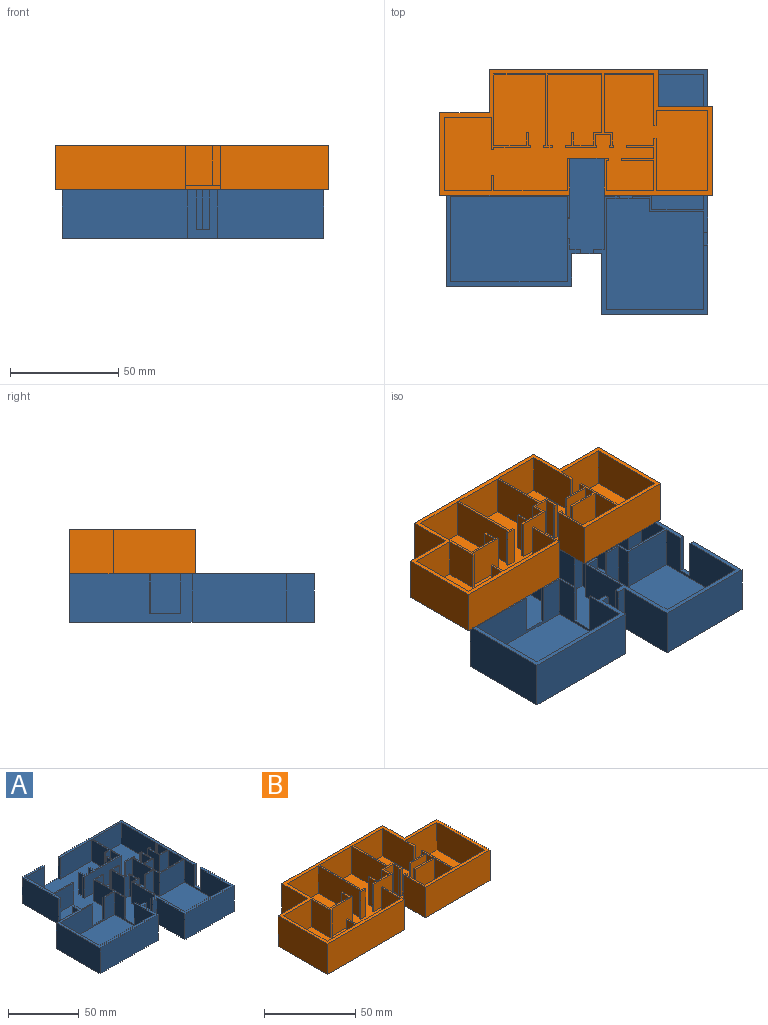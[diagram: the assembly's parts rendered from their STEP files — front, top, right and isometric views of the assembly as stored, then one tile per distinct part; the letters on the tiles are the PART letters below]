
ASSEMBLY  parts=2 mates=1
PART A: 128 faces, bbox 121x113x22.4 mm
  f0: plane 97x85mm, normal (0,0,1), area 5730mm2, adj f5,f6,f11,f17,f18,f19,f20,f21
  f1: plane 6x2mm, normal (0,0,1), area 12mm2, adj f4,f13,f14,f49
  f2: plane 28x22.4mm, normal (-1,0,0), area 627.2mm2, adj f3,f11,f12,f35
  f3: plane 49x22.4mm, normal (0,-1,0), area 1097.6mm2, adj f2,f4,f12,f35
  f4: plane 113x22.4mm, normal (1,0,0), area 2420.8mm2, adj f1,f3,f5,f12,f13,f35,f49,f107
  f5: plane 99x22.4mm, normal (0,1,0), area 1941.6mm2, adj f0,f4,f6,f12,f50,f107,f109,f116
  f6: plane 56.5x22.4mm, normal (-1,0,0), area 1008mm2, adj f0,f5,f7,f12,f37,f48,f110,f116
  f7: plane 22.4x22mm, normal (0,1,0), area 492.8mm2, adj f6,f8,f12,f48
  f8: plane 43.5x22.4mm, normal (-1,0,0), area 974.4mm2, adj f7,f9,f12,f48
  f9: plane 58x22.4mm, normal (0,-1,0), area 1299.2mm2, adj f8,f10,f12,f48
  f10: plane 22.4x15mm, normal (1,0,0), area 336mm2, adj f9,f11,f12,f48
  f11: plane 22.4x14mm, normal (0,-1,0), area 203.2mm2, adj f0,f2,f10,f12,f34,f35,f38,f48
  f12: plane 121x113mm, normal (0,0,-1), area 11284mm2, adj f2,f3,f4,f5,f6,f7,f8,f9
  f13: plane 18.4x2mm, normal (0,1,0), area 36.8mm2, adj f1,f4,f14,f35
  f14: plane 45.5x19.8mm, normal (-1,0,0), area 790.5mm2, adj f1,f13,f15,f35,f49,f106,f107,f126
  f15: plane 45x19.8mm, normal (0,1,0), area 891mm2, adj f14,f16,f35,f126
  f16: plane 51.5x19.8mm, normal (1,0,0), area 1019.7mm2, adj f15,f17,f35,f126
  f17: plane 20x19.8mm, normal (0,-1,0), area 285.6mm2, adj f0,f16,f18,f35,f104,f105,f107,f126
  f18: plane 18.4x1mm, normal (1,0,0), area 18.4mm2, adj f0,f17,f19,f35
  f19: plane 18.4x1mm, normal (0,1,0), area 18.4mm2, adj f0,f18,f20,f35
  f20: plane 18.4x8mm, normal (1,0,0), area 147.2mm2, adj f0,f19,f21,f35
  f21: plane 18.4x5mm, normal (0,1,0), area 92mm2, adj f0,f20,f22,f35
  f22: plane 18.4x12mm, normal (1,0,0), area 220.8mm2, adj f0,f21,f23,f35
  f23: plane 18.4x7mm, normal (0,-1,0), area 128.8mm2, adj f0,f22,f24,f35
  f24: plane 18.4x1mm, normal (1,0,0), area 18.4mm2, adj f0,f23,f25,f35
  f25: plane 18.4x9mm, normal (0,1,0), area 165.6mm2, adj f0,f24,f26,f35
  f26: plane 18.4x1mm, normal (-1,0,0), area 18.4mm2, adj f0,f25,f27,f35
  f27: plane 18.4x1mm, normal (0,-1,0), area 18.4mm2, adj f0,f26,f28,f35
  f28: plane 18.4x13mm, normal (-1,0,0), area 239.2mm2, adj f0,f27,f29,f35
  f29: plane 18.4x5mm, normal (0,-1,0), area 92mm2, adj f0,f28,f30,f35
  f30: plane 18.4x7mm, normal (-1,0,0), area 128.8mm2, adj f0,f29,f31,f35
  f31: plane 18.4x5mm, normal (0,1,0), area 92mm2, adj f0,f30,f32,f35
  f32: plane 24.5x18.4mm, normal (-1,0,0), area 450.8mm2, adj f0,f31,f33,f35
  f33: plane 18.4x5mm, normal (0,1,0), area 92mm2, adj f0,f32,f34,f35
  f34: plane 18.4x2mm, normal (-1,0,0), area 36.8mm2, adj f0,f11,f33,f35
  f35: plane 75.5x53mm, normal (0,0,1), area 286.5mm2, adj f2,f3,f4,f11,f13,f14,f15,f16
  f36: plane 18.4x6.5mm, normal (1,0,0), area 119.6mm2, adj f0,f37,f47,f48
  f37: plane 18.4x2mm, normal (0,1,0), area 36.8mm2, adj f0,f6,f36,f48
  f38: plane 18.4x2mm, normal (1,0,0), area 36.8mm2, adj f0,f11,f39,f48
  f39: plane 18.4x5mm, normal (0,1,0), area 92mm2, adj f0,f38,f40,f48
  f40: plane 18.4x5mm, normal (1,0,0), area 92mm2, adj f0,f39,f41,f48
  f41: plane 18.4x1mm, normal (0,1,0), area 18.4mm2, adj f0,f40,f42,f48
  f42: plane 39.5x19.8mm, normal (-1,0,0), area 607.3mm2, adj f0,f41,f43,f45,f48,f117,f125,f127
  f43: plane 54x19.8mm, normal (0,1,0), area 1069.2mm2, adj f42,f44,f48,f127
  f44: plane 39.5x19.8mm, normal (1,0,0), area 782.1mm2, adj f43,f45,f48,f127
  f45: plane 54x19.8mm, normal (0,-1,0), area 866.8mm2, adj f0,f42,f44,f46,f48,f124,f125,f127
  f46: plane 18.4x1mm, normal (1,0,0), area 18.4mm2, adj f0,f45,f47,f48
  f47: plane 18.4x10.5mm, normal (0,1,0), area 193.2mm2, adj f0,f36,f46,f48
  f48: plane 62x49mm, normal (0,0,1), area 307.5mm2, adj f6,f7,f8,f9,f10,f11,f36,f37
  f49: plane 18.4x2mm, normal (0,-1,0), area 36.8mm2, adj f1,f4,f14,f107
  f50: plane 18.4x2mm, normal (-1,0,0), area 36.8mm2, adj f0,f5,f51,f107
  f51: plane 31.5x18.4mm, normal (0,-1,0), area 579.6mm2, adj f0,f50,f52,f107
  f52: plane 18.4x17.5mm, normal (-1,0,0), area 322mm2, adj f0,f51,f53,f107
  f53: plane 18.4x4.5mm, normal (0,1,0), area 82.8mm2, adj f0,f52,f54,f107
  f54: plane 18.4x1mm, normal (-1,0,0), area 18.4mm2, adj f0,f53,f55,f107
  f55: plane 18.4x4.5mm, normal (0,-1,0), area 82.8mm2, adj f0,f54,f56,f107
  f56: plane 18.4x9mm, normal (-1,0,0), area 165.6mm2, adj f0,f55,f57,f107
  f57: plane 18.4x6.5mm, normal (0,1,0), area 119.6mm2, adj f0,f56,f58,f107
  f58: plane 18.4x5mm, normal (1,0,0), area 92mm2, adj f0,f57,f59,f107
  f59: plane 18.4x1mm, normal (0,1,0), area 18.4mm2, adj f0,f58,f60,f107
  f60: plane 18.4x5mm, normal (-1,0,0), area 92mm2, adj f0,f59,f61,f107
  f61: plane 18.4x17.5mm, normal (0,1,0), area 322mm2, adj f0,f60,f62,f107
  f62: plane 18.4x5mm, normal (1,0,0), area 92mm2, adj f0,f61,f63,f107
  f63: plane 18.4x1mm, normal (0,1,0), area 18.4mm2, adj f0,f62,f64,f107
  f64: plane 18.4x5mm, normal (-1,0,0), area 92mm2, adj f0,f63,f65,f107
  f65: plane 18.4x8mm, normal (0,1,0), area 147.2mm2, adj f0,f64,f66,f107
  f66: plane 18.4x5mm, normal (1,0,0), area 92mm2, adj f0,f65,f67,f107
  f67: plane 18.4x1mm, normal (0,1,0), area 18.4mm2, adj f0,f66,f68,f107
  f68: plane 18.4x5mm, normal (-1,0,0), area 92mm2, adj f0,f67,f69,f107
  f69: plane 18.4x1mm, normal (0,1,0), area 18.4mm2, adj f0,f68,f70,f107
  f70: plane 18.4x1mm, normal (-1,0,0), area 18.4mm2, adj f0,f69,f71,f107
  f71: plane 37x18.4mm, normal (0,-1,0), area 680.8mm2, adj f0,f70,f72,f107
  f72: plane 28.5x18.4mm, normal (1,0,0), area 524.4mm2, adj f0,f71,f73,f107
  f73: plane 28.5x18.4mm, normal (0,-1,0), area 524.4mm2, adj f0,f72,f74,f107
  f74: plane 35.5x18.4mm, normal (-1,0,0), area 653.2mm2, adj f0,f73,f75,f107
  f75: plane 18.4x1mm, normal (0,1,0), area 18.4mm2, adj f0,f74,f76,f107
  f76: plane 18.4x1mm, normal (-1,0,0), area 18.4mm2, adj f0,f75,f77,f107
  f77: plane 18.4x1mm, normal (0,-1,0), area 18.4mm2, adj f0,f76,f78,f107
  f78: plane 18.4x10mm, normal (-1,0,0), area 184mm2, adj f0,f77,f79,f107
  f79: plane 18.4x8mm, normal (0,1,0), area 147.2mm2, adj f0,f78,f80,f107
  f80: plane 18.4x10mm, normal (1,0,0), area 184mm2, adj f0,f79,f81,f107
  f81: plane 18.4x1mm, normal (0,-1,0), area 18.4mm2, adj f0,f80,f82,f107
  f82: plane 18.4x1mm, normal (1,0,0), area 18.4mm2, adj f0,f81,f83,f107
  f83: plane 18.4x2mm, normal (0,1,0), area 36.8mm2, adj f0,f82,f84,f107
  f84: plane 18.4x12mm, normal (-1,0,0), area 220.8mm2, adj f0,f83,f85,f107
  f85: plane 18.4x9mm, normal (0,-1,0), area 165.6mm2, adj f0,f84,f86,f107
  f86: plane 18.4x15mm, normal (-1,0,0), area 276mm2, adj f0,f85,f87,f107
  f87: plane 24x18.4mm, normal (0,1,0), area 441.6mm2, adj f0,f86,f88,f107
  f88: plane 18.4x15mm, normal (1,0,0), area 276mm2, adj f0,f87,f89,f107
  f89: plane 18.4x9mm, normal (0,-1,0), area 165.6mm2, adj f0,f88,f90,f107
  f90: plane 18.4x12mm, normal (1,0,0), area 220.8mm2, adj f0,f89,f91,f107
  f91: plane 18.4x2mm, normal (0,1,0), area 36.8mm2, adj f0,f90,f92,f107
  f92: plane 18.4x1mm, normal (-1,0,0), area 18.4mm2, adj f0,f91,f93,f107
  f93: plane 18.4x1mm, normal (0,-1,0), area 18.4mm2, adj f0,f92,f94,f107
  f94: plane 18.4x10mm, normal (-1,0,0), area 184mm2, adj f0,f93,f95,f107
  f95: plane 18.4x8mm, normal (0,1,0), area 147.2mm2, adj f0,f94,f96,f107
  f96: plane 18.4x10mm, normal (1,0,0), area 184mm2, adj f0,f95,f97,f107
  f97: plane 18.4x1mm, normal (0,-1,0), area 18.4mm2, adj f0,f96,f98,f107
  f98: plane 18.4x1mm, normal (1,0,0), area 18.4mm2, adj f0,f97,f99,f107
  f99: plane 18.4x9mm, normal (0,1,0), area 165.6mm2, adj f0,f98,f100,f107
  f100: plane 18.4x1mm, normal (-1,0,0), area 18.4mm2, adj f0,f99,f101,f107
  f101: plane 18.4x7mm, normal (0,-1,0), area 128.8mm2, adj f0,f100,f102,f107
  f102: plane 20x18.4mm, normal (-1,0,0), area 368mm2, adj f0,f101,f103,f107
  f103: plane 18.4x8mm, normal (0,1,0), area 147.2mm2, adj f0,f102,f104,f107
  f104: plane 18.4x1mm, normal (-1,0,0), area 18.4mm2, adj f0,f17,f103,f107
  f105: plane 19.8x6mm, normal (-1,0,0), area 118.8mm2, adj f17,f106,f107,f126
  f106: plane 25x19.8mm, normal (0,-1,0), area 495mm2, adj f14,f105,f107,f126
  f107: plane 75x67.5mm, normal (0,0,1), area 467mm2, adj f4,f5,f14,f17,f49,f50,f51,f52
  f108: plane 19x18.4mm, normal (0,-1,0), area 349.6mm2, adj f0,f109,f115,f116
  f109: plane 18.4x2mm, normal (1,0,0), area 36.8mm2, adj f0,f5,f108,f116
  f110: plane 18.4x2mm, normal (0,-1,0), area 36.8mm2, adj f0,f6,f111,f116
  f111: plane 18.4x6.5mm, normal (1,0,0), area 119.6mm2, adj f0,f110,f112,f116
  f112: plane 19x18.4mm, normal (0,-1,0), area 349.6mm2, adj f0,f111,f113,f116
  f113: plane 18.4x1mm, normal (1,0,0), area 18.4mm2, adj f0,f112,f114,f116
  f114: plane 19x18.4mm, normal (0,1,0), area 349.6mm2, adj f0,f113,f115,f116
  f115: plane 27.5x18.4mm, normal (1,0,0), area 506mm2, adj f0,f108,f114,f116
  f116: plane 37x21mm, normal (0,0,1), area 131mm2, adj f5,f6,f108,f109,f110,f111,f112,f113
  f117: plane 18.4x1mm, normal (0,-1,0), area 18.4mm2, adj f0,f42,f118,f125
  f118: plane 30x18.4mm, normal (1,0,0), area 552mm2, adj f0,f117,f119,f125
  f119: plane 18.4x8mm, normal (0,-1,0), area 147.2mm2, adj f0,f118,f120,f125
  f120: plane 18.4x1mm, normal (1,0,0), area 18.4mm2, adj f0,f119,f121,f125
  f121: plane 18.4x9mm, normal (0,1,0), area 165.6mm2, adj f0,f120,f122,f125
  f122: plane 20x18.4mm, normal (-1,0,0), area 368mm2, adj f0,f121,f123,f125
  f123: plane 18.4x10.5mm, normal (0,1,0), area 193.2mm2, adj f0,f122,f124,f125
  f124: plane 18.4x1mm, normal (-1,0,0), area 18.4mm2, adj f0,f45,f123,f125
  f125: plane 31x19.5mm, normal (0,0,1), area 49.5mm2, adj f42,f45,f117,f118,f119,f120,f121,f122
  f126: plane 51.5x45mm, normal (0,0,1), area 2167.5mm2, adj f14,f15,f16,f17,f105,f106
  f127: plane 54x39.5mm, normal (0,0,1), area 2133mm2, adj f42,f43,f44,f45
PART B: 90 faces, bbox 126x58x20.4 mm
  f0: plane 60x20.4mm, normal (0,-1,0), area 1224mm2, adj f1,f2,f4,f75
  f1: plane 126x58mm, normal (0,0,1), area 928mm2, adj f0,f4,f5,f6,f7,f8,f9,f10
  f2: plane 126x58mm, normal (0,0,-1), area 6151mm2, adj f0,f4,f5,f6,f7,f8,f9,f10
  f3: plane 122x54mm, normal (0,0,1), area 5223mm2, adj f12,f13,f14,f15,f16,f17,f18,f19
  f4: plane 38x20.4mm, normal (-1,0,0), area 775.2mm2, adj f0,f1,f2,f11
  f5: plane 50x20.4mm, normal (0,-1,0), area 1020mm2, adj f1,f2,f6,f74
  f6: plane 41x20.4mm, normal (1,0,0), area 836.4mm2, adj f1,f2,f5,f7
  f7: plane 25x20.4mm, normal (0,1,0), area 510mm2, adj f1,f2,f6,f8
  f8: plane 20.4x17mm, normal (1,0,0), area 346.8mm2, adj f1,f2,f7,f9
  f9: plane 78x20.4mm, normal (0,1,0), area 1591.2mm2, adj f1,f2,f8,f10
  f10: plane 20.4x20mm, normal (-1,0,0), area 408mm2, adj f1,f2,f9,f11
  f11: plane 23x20.4mm, normal (0,1,0), area 469.2mm2, adj f1,f2,f4,f10
  f12: plane 18.4x1mm, normal (1,0,0), area 18.4mm2, adj f1,f3,f13,f88
  f13: plane 18.4x1mm, normal (0,1,0), area 18.4mm2, adj f1,f3,f12,f14
  f14: plane 18.4x6mm, normal (1,0,0), area 110.4mm2, adj f1,f3,f13,f15
  f15: plane 18.4x1mm, normal (0,1,0), area 18.4mm2, adj f1,f3,f14,f16
  f16: plane 18.4x6mm, normal (-1,0,0), area 110.4mm2, adj f1,f3,f15,f17
  f17: plane 18.4x15mm, normal (0,1,0), area 276mm2, adj f1,f3,f16,f18
  f18: plane 33x18.4mm, normal (1,0,0), area 607.2mm2, adj f1,f3,f17,f19
  f19: plane 24x18.4mm, normal (0,-1,0), area 441.6mm2, adj f1,f3,f18,f20
  f20: plane 33x18.4mm, normal (-1,0,0), area 607.2mm2, adj f1,f3,f19,f21
  f21: plane 18.4x1mm, normal (0,1,0), area 18.4mm2, adj f1,f3,f20,f22
  f22: plane 18.4x1mm, normal (-1,0,0), area 18.4mm2, adj f1,f3,f21,f23
  f23: plane 18.4x4mm, normal (0,-1,0), area 73.6mm2, adj f1,f3,f22,f24
  f24: plane 18.4x1mm, normal (1,0,0), area 18.4mm2, adj f1,f3,f23,f25
  f25: plane 18.4x2mm, normal (0,1,0), area 36.8mm2, adj f1,f3,f24,f26
  f26: plane 33x18.4mm, normal (1,0,0), area 607.2mm2, adj f1,f3,f25,f27
  f27: plane 25x18.4mm, normal (0,-1,0), area 460mm2, adj f1,f3,f26,f28
  f28: plane 27x18.4mm, normal (-1,0,0), area 496.8mm2, adj f1,f3,f27,f29
  f29: plane 18.4x4mm, normal (0,1,0), area 73.6mm2, adj f1,f3,f28,f30
  f30: plane 18.4x6mm, normal (-1,0,0), area 110.4mm2, adj f1,f3,f29,f31
  f31: plane 18.4x9mm, normal (0,1,0), area 165.6mm2, adj f1,f3,f30,f32
  f32: plane 18.4x6mm, normal (1,0,0), area 110.4mm2, adj f1,f3,f31,f33
  f33: plane 18.4x1mm, normal (0,1,0), area 18.4mm2, adj f1,f3,f32,f34
  f34: plane 18.4x6mm, normal (-1,0,0), area 110.4mm2, adj f1,f3,f33,f35
  f35: plane 18.4x3mm, normal (0,1,0), area 55.2mm2, adj f1,f3,f34,f36
  f36: plane 18.4x1mm, normal (-1,0,0), area 18.4mm2, adj f1,f3,f35,f37
  f37: plane 18.4x14.5mm, normal (0,-1,0), area 266.8mm2, adj f1,f3,f36,f38
  f38: plane 18.4x1mm, normal (1,0,0), area 18.4mm2, adj f1,f3,f37,f39
  f39: plane 18.4x0.5mm, normal (0,1,0), area 9.2mm2, adj f1,f3,f38,f40
  f40: plane 18.4x5mm, normal (1,0,0), area 92mm2, adj f1,f3,f39,f41
  f41: plane 18.4x7mm, normal (0,-1,0), area 128.8mm2, adj f1,f3,f40,f42
  f42: plane 18.4x5mm, normal (-1,0,0), area 92mm2, adj f1,f3,f41,f43
  f43: plane 18.4x0.5mm, normal (0,1,0), area 9.2mm2, adj f1,f3,f42,f44
  f44: plane 18.4x1mm, normal (-1,0,0), area 18.4mm2, adj f1,f3,f43,f45
  f45: plane 18.4x2mm, normal (0,-1,0), area 36.8mm2, adj f1,f3,f44,f46
  f46: plane 18.4x1mm, normal (1,0,0), area 18.4mm2, adj f1,f3,f45,f47
  f47: plane 18.4x0.5mm, normal (0,1,0), area 9.2mm2, adj f1,f3,f46,f48
  f48: plane 18.4x6mm, normal (1,0,0), area 110.4mm2, adj f1,f3,f47,f49
  f49: plane 18.4x4mm, normal (0,1,0), area 73.6mm2, adj f1,f3,f48,f50
  f50: plane 27x18.4mm, normal (1,0,0), area 496.8mm2, adj f1,f3,f49,f51
  f51: plane 23x18.4mm, normal (0,-1,0), area 423.2mm2, adj f1,f3,f50,f52
  f52: plane 24x18.4mm, normal (-1,0,0), area 441.6mm2, adj f1,f3,f51,f53
  f53: plane 18.4x1mm, normal (0,-1,0), area 18.4mm2, adj f1,f3,f52,f54
  f54: plane 18.4x7mm, normal (1,0,0), area 128.8mm2, adj f1,f3,f53,f55
  f55: plane 24x18.4mm, normal (0,-1,0), area 441.6mm2, adj f1,f3,f54,f56
  f56: plane 37x18.4mm, normal (-1,0,0), area 680.8mm2, adj f1,f3,f55,f57
  f57: plane 24x18.4mm, normal (0,1,0), area 441.6mm2, adj f1,f3,f56,f58
  f58: plane 24x18.4mm, normal (1,0,0), area 441.6mm2, adj f1,f3,f57,f59
  f59: plane 18.4x1mm, normal (0,1,0), area 18.4mm2, adj f1,f3,f58,f60
  f60: plane 18.4x3mm, normal (-1,0,0), area 55.2mm2, adj f1,f3,f59,f61
  f61: plane 18.4x12.5mm, normal (0,1,0), area 230mm2, adj f1,f3,f60,f62
  f62: plane 18.4x1mm, normal (-1,0,0), area 18.4mm2, adj f1,f3,f61,f63
  f63: plane 18.4x12.5mm, normal (0,-1,0), area 230mm2, adj f1,f3,f62,f64
  f64: plane 18.4x5mm, normal (-1,0,0), area 92mm2, adj f1,f3,f63,f65
  f65: plane 18.4x15mm, normal (0,1,0), area 276mm2, adj f1,f3,f64,f66
  f66: plane 18.4x1mm, normal (-1,0,0), area 18.4mm2, adj f1,f3,f65,f67
  f67: plane 18.4x15mm, normal (0,-1,0), area 276mm2, adj f1,f3,f66,f68
  f68: plane 18.4x14mm, normal (-1,0,0), area 257.6mm2, adj f1,f3,f67,f69
  f69: plane 22x18.4mm, normal (0,1,0), area 404.8mm2, adj f1,f3,f68,f70
  f70: plane 18.4x14mm, normal (1,0,0), area 257.6mm2, adj f1,f3,f69,f71
  f71: plane 18.4x1mm, normal (0,-1,0), area 18.4mm2, adj f1,f3,f70,f72
  f72: plane 18.4x1mm, normal (1,0,0), area 18.4mm2, adj f1,f3,f71,f73
  f73: plane 18.4x2mm, normal (0,1,0), area 36.8mm2, adj f1,f3,f72,f74
  f74: plane 20.4x17mm, normal (-1,0,0), area 346.8mm2, adj f1,f2,f5,f73,f89
  f75: plane 20.4x17mm, normal (1,0,0), area 346.8mm2, adj f0,f1,f2,f76,f89
  f76: plane 18.4x1mm, normal (0,1,0), area 18.4mm2, adj f1,f3,f75,f77
  f77: plane 18.4x15mm, normal (-1,0,0), area 276mm2, adj f1,f3,f76,f78
  f78: plane 34x18.4mm, normal (0,1,0), area 625.6mm2, adj f1,f3,f77,f79
  f79: plane 18.4x7mm, normal (1,0,0), area 128.8mm2, adj f1,f3,f78,f80
  f80: plane 18.4x1mm, normal (0,1,0), area 18.4mm2, adj f1,f3,f79,f81
  f81: plane 18.4x7mm, normal (-1,0,0), area 128.8mm2, adj f1,f3,f80,f82
  f82: plane 22x18.4mm, normal (0,1,0), area 404.8mm2, adj f1,f3,f81,f83
  f83: plane 34x18.4mm, normal (1,0,0), area 625.6mm2, adj f1,f3,f82,f84
  f84: plane 22x18.4mm, normal (0,-1,0), area 404.8mm2, adj f1,f3,f83,f85
  f85: plane 18.4x15mm, normal (-1,0,0), area 276mm2, adj f1,f3,f84,f86
  f86: plane 18.4x1mm, normal (0,-1,0), area 18.4mm2, adj f1,f3,f85,f87
  f87: plane 18.4x1mm, normal (1,0,0), area 18.4mm2, adj f1,f3,f86,f88
  f88: plane 18.4x17mm, normal (0,-1,0), area 312.8mm2, adj f1,f3,f12,f87
  f89: plane 16x2mm, normal (0,-1,0), area 32mm2, adj f2,f3,f74,f75
PLACE A t=(-14.76,-22.38,38.06)mm fixed
PLACE B t=(-30.39,32.62,62.46)mm
MATE fastened B.f9 <-> A.f5  axis (0,1,0) through (-66.76,90.62,60.46)mm
